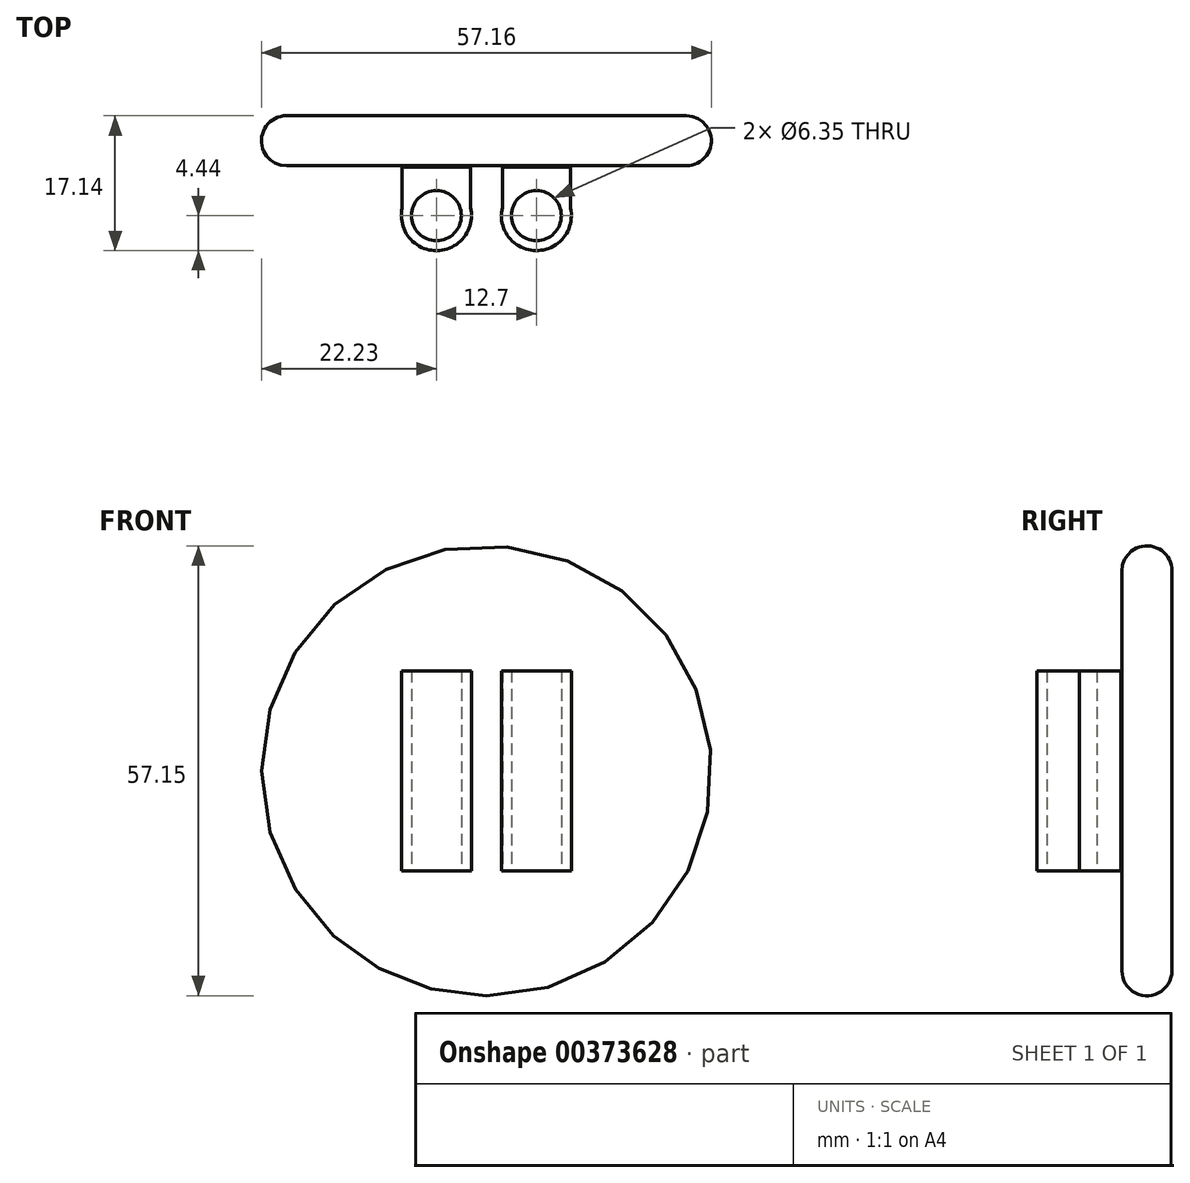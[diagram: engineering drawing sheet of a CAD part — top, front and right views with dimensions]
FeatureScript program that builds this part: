
annotation { "Feature Type Name" : "Feature", "Feature Type Description" : "" }
export const myFeature = defineFeature(function(context is Context, id is Id, definition is map)
    precondition{}
    {
        {
            var Q0;
            Q0=qCreatedBy(makeId("Front.planeOp"),FACE);
            var sketch = newSketch(context, id + "F0", { "sketchPlane" : qUnion([Q0])});
            skCircle(sketch, "E0", {"center": v(0, 0) * mm, "radius": 28.58 * mm});
            skSolve(sketch);
        }
        {
            var Q0;
            Q0 = qSketchRegion(id + "F0", true);
            extrude(context, id + "F1", {"entities" : qUnion([Q0]), "depth" : 6.35 * mm});
        }
        {
            var Q0;
            Q0=makeQuery(id+"F1.opExtrude","CAP_EDGE",EDGE,{"disambiguationData":[OSD([sQuery(id+"F0.wireOp",EDGE,"E0")])],"isStart":false});
            var Q1;
            Q1=makeQuery(id+"F1.opExtrude","SWEPT_FACE",FACE,{"disambiguationData":[OSD([sQuery(id+"F0.wireOp",EDGE,"E0")])]});
            fillet(context, id + "F2", {"entities" : qUnion([Q0, Q1]), "radius" : 3.17 * mm, "tangentPropagation" : true, "allowEdgeOverflow" : false});
        }
        {
            var Q0;
            Q0=qCreatedBy(makeId("Top.planeOp"),FACE);
            var sketch = newSketch(context, id + "F3", { "sketchPlane" : qUnion([Q0])});
            skCircle(sketch, "E1", {"center": v(6.35, -12.7) * mm, "radius": 3.18 * mm});
            skCircle(sketch, "E2", {"center": v(6.35, -12.7) * mm, "radius": 4.45 * mm});
            skLineSegment(sketch, "E3", {"start": v(2.03, -11.66) * mm, "end": v(2.03, -6.5) * mm});
            skLineSegment(sketch, "E4", {"start": v(10.7, -11.75) * mm, "end": v(10.7, -6.5) * mm});
            skLineSegment(sketch, "E5", {"start": v(2.03, -6.5) * mm, "end": v(10.7, -6.5) * mm});
            skLineSegment(sketch, "E6.MirrorCS", {"start": v(-2.03, -11.66) * mm, "end": v(-2.03, -6.5) * mm});
            skCircle(sketch, "E7.MirrorC", {"center": v(-6.35, -12.7) * mm, "radius": 4.45 * mm});
            skCircle(sketch, "E8.MirrorC", {"center": v(-6.35, -12.7) * mm, "radius": 3.18 * mm});
            skLineSegment(sketch, "E9.MirrorCS", {"start": v(-2.03, -6.5) * mm, "end": v(-10.7, -6.5) * mm});
            skLineSegment(sketch, "E10.MirrorCS", {"start": v(-10.7, -11.75) * mm, "end": v(-10.7, -6.5) * mm});
            skSolve(sketch);
        }
        {
            var Q0;
            Q0 = qSketchRegion(id + "F3", true);
            extrude(context, id + "F4", {"entities" : qUnion([Q0]), "depth" : 12.7 * mm, "hasSecondDirection" : true, "secondDirectionOppositeDirection" : true, "secondDirectionDepth" : 12.7 * mm});
        }
    });
